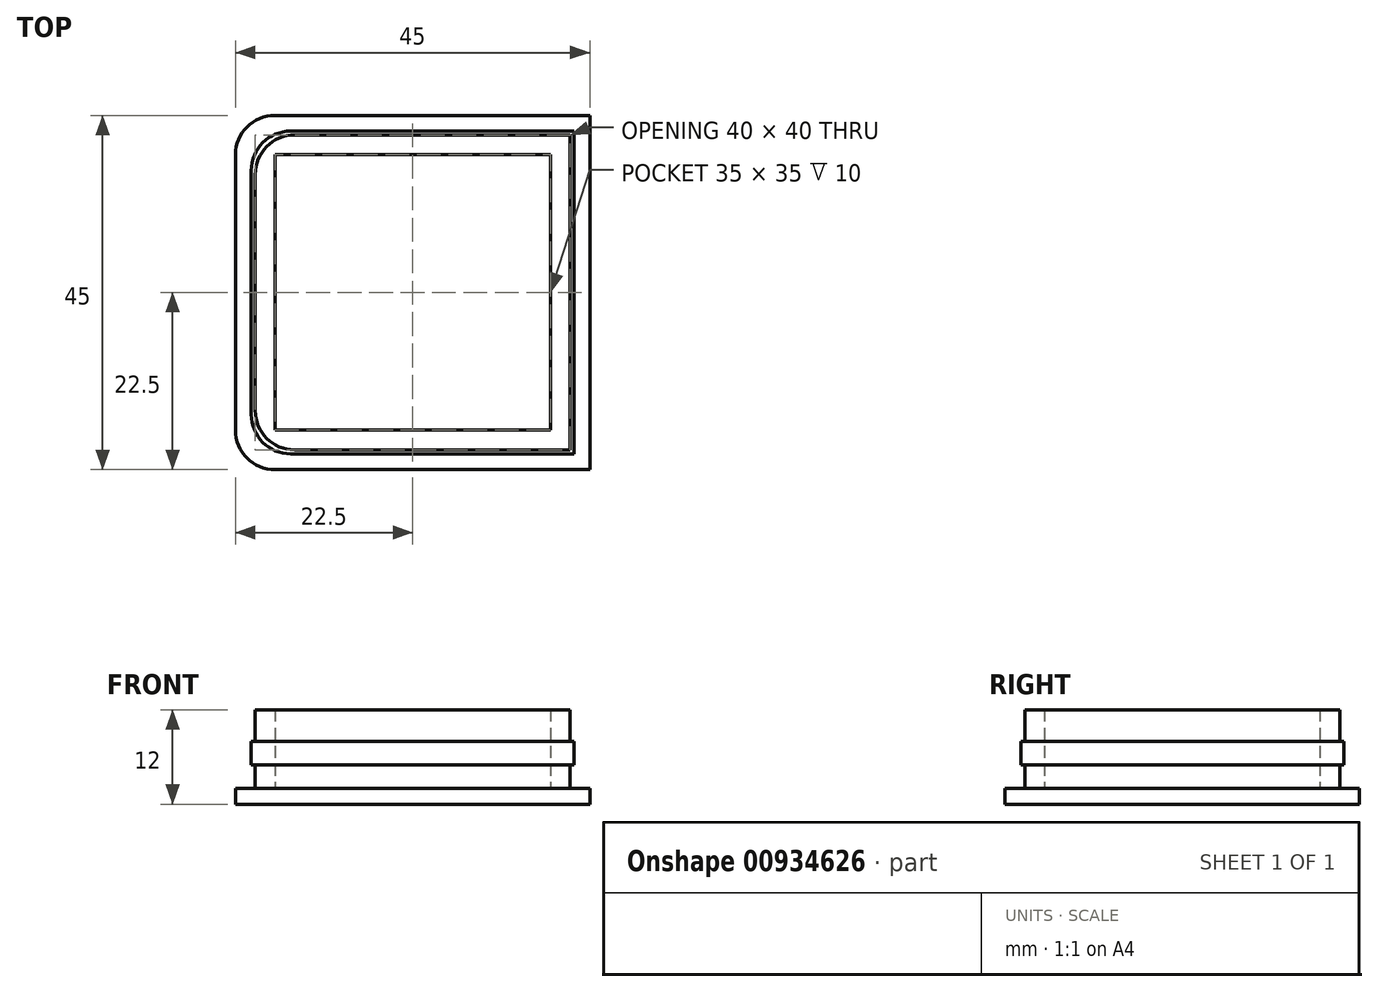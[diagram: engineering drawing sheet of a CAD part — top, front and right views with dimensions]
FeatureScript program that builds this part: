
annotation { "Feature Type Name" : "Feature", "Feature Type Description" : "" }
export const myFeature = defineFeature(function(context is Context, id is Id, definition is map)
    precondition{}
    {
        {
            var Q0;
            Q0=qCreatedBy(makeId("Top.planeOp"),FACE);
            var sketch = newSketch(context, id + "F0", { "sketchPlane" : qUnion([Q0])});
            skLineSegment(sketch, "E0.bottom", {"start": v(22.5, -22.5) * mm, "end": v(-22.5, -22.5) * mm});
            skLineSegment(sketch, "E0.top", {"start": v(22.5, 22.5) * mm, "end": v(-22.5, 22.5) * mm});
            skLineSegment(sketch, "E0.left", {"start": v(22.5, -22.5) * mm, "end": v(22.5, 22.5) * mm});
            skLineSegment(sketch, "E0.right", {"start": v(-22.5, -22.5) * mm, "end": v(-22.5, 22.5) * mm});
            skPoint(sketch, "E0.middle", {"position": v(0, 0) * mm});
            skSolve(sketch);
        }
        {
            var Q0;
            Q0=makeQuery(id+"F0.imprint","IMPRINT",FACE,{"disambiguationData":[TD([[makeQuery(id+"F0.imprint","IMPRINT",EDGE,{"derivedFrom":sQuery(id+"F0.wireOp",EDGE,"E0.bottom")}),-1.0]])]});
            extrude(context, id + "F1", {"entities" : qUnion([Q0]), "depth" : 2 * mm, "offsetDistance" : 25 * mm});
        }
        {
            var Q0;
            Q0=makeQuery(id+"F1.opExtrude","CAP_FACE",FACE,{"disambiguationData":[OSD([sQuery(id+"F0.wireOp",EDGE,"E0.bottom"),sQuery(id+"F0.wireOp",EDGE,"E0.top"),sQuery(id+"F0.wireOp",EDGE,"E0.left"),sQuery(id+"F0.wireOp",EDGE,"E0.right")])],"isStart":false});
            var sketch = newSketch(context, id + "F2", { "sketchPlane" : qUnion([Q0])});
            skLineSegment(sketch, "E1.bottom", {"start": v(-20, -20) * mm, "end": v(20, -20) * mm});
            skLineSegment(sketch, "E1.top", {"start": v(-20, 20) * mm, "end": v(20, 20) * mm});
            skLineSegment(sketch, "E1.left", {"start": v(-20, -20) * mm, "end": v(-20, 20) * mm});
            skLineSegment(sketch, "E1.right", {"start": v(20, -20) * mm, "end": v(20, 20) * mm});
            skPoint(sketch, "E1.middle", {"position": v(0, 0) * mm});
            skLineSegment(sketch, "E2.bottom", {"start": v(-17.5, -17.5) * mm, "end": v(17.5, -17.5) * mm});
            skLineSegment(sketch, "E2.top", {"start": v(-17.5, 17.5) * mm, "end": v(17.5, 17.5) * mm});
            skLineSegment(sketch, "E2.left", {"start": v(-17.5, -17.5) * mm, "end": v(-17.5, 17.5) * mm});
            skLineSegment(sketch, "E2.right", {"start": v(17.5, -17.5) * mm, "end": v(17.5, 17.5) * mm});
            skSolve(sketch);
        }
        {
            var Q0;
            Q0=makeQuery(id+"F2.imprint","IMPRINT",FACE,{"disambiguationData":[TD([[makeQuery(id+"F2.imprint","IMPRINT",EDGE,{"derivedFrom":sQuery(id+"F2.wireOp",EDGE,"E1.bottom")}),1.0]])]});
            extrude(context, id + "F3", {"entities" : qUnion([Q0]), "operationType" : NewBodyOperationType.ADD, "depth" : 10 * mm, "offsetDistance" : 25 * mm});
        }
        {
            var Q0;
            Q0=makeQuery(id+"F3.boolean.opBoolean","SPLIT",FACE,{"disambiguationData":[TD([makeQuery(id+"F3.opExtrude","SWEPT_FACE",FACE,{"disambiguationData":[OSD([sQuery(id+"F2.wireOp",EDGE,"E2.bottom")])]})])],"derivedFrom":makeQuery(id+"F1.opExtrude","CAP_FACE",FACE,{"disambiguationData":[OSD([sQuery(id+"F0.wireOp",EDGE,"E0.bottom"),sQuery(id+"F0.wireOp",EDGE,"E0.top"),sQuery(id+"F0.wireOp",EDGE,"E0.left"),sQuery(id+"F0.wireOp",EDGE,"E0.right")])],"isStart":false})});
            var sketch = newSketch(context, id + "F4", { "sketchPlane" : qUnion([Q0])});
            skLineSegment(sketch, "E3.bottom", {"start": v(-20.5, -20.5) * mm, "end": v(20.5, -20.5) * mm});
            skLineSegment(sketch, "E3.top", {"start": v(-20.5, 20.5) * mm, "end": v(20.5, 20.5) * mm});
            skLineSegment(sketch, "E3.left", {"start": v(-20.5, -20.5) * mm, "end": v(-20.5, 20.5) * mm});
            skLineSegment(sketch, "E3.right", {"start": v(20.5, -20.5) * mm, "end": v(20.5, 20.5) * mm});
            skPoint(sketch, "E3.middle", {"position": v(0, 0) * mm});
            skSolve(sketch);
        }
        {
            var Q0;
            Q0=makeQuery(id+"F4.imprint","IMPRINT",FACE,{"disambiguationData":[TD([[makeQuery(id+"F4.imprint","IMPRINT",EDGE,{"derivedFrom":sQuery(id+"F4.wireOp",EDGE,"E3.bottom")}),1.0]])]});
            extrude(context, id + "F5", {"entities" : qUnion([Q0]), "operationType" : NewBodyOperationType.ADD, "depth" : 6 * mm, "offsetDistance" : 25 * mm, "hasSecondDirection" : true, "secondDirectionOppositeDirection" : true, "secondDirectionDepth" : -3 * mm});
        }
        {
            var Q0;
            Q0=makeQuery(id+"F1.opExtrude","SWEPT_EDGE",EDGE,{"disambiguationData":[OSD([sQuery(id+"F0.wireOp",EDGE,"E0.top"),sQuery(id+"F0.wireOp",EDGE,"E0.right")])]});
            var Q1;
            {var subQ0=sQuery(id+"F2.wireOp",EDGE,"E1.left");var subQ1=sQuery(id+"F2.wireOp",EDGE,"E1.top");Q1=makeQuery(id+"F5.boolean.opBoolean","SPLIT",EDGE,{"disambiguationData":[TD([makeQuery(id+"F1.opExtrude","CAP_FACE",FACE,{"disambiguationData":[OSD([sQuery(id+"F0.wireOp",EDGE,"E0.bottom"),sQuery(id+"F0.wireOp",EDGE,"E0.top"),sQuery(id+"F0.wireOp",EDGE,"E0.left"),sQuery(id+"F0.wireOp",EDGE,"E0.right")])],"isStart":false})])],"derivedFrom":makeQuery(id+"F3.opExtrude","SWEPT_EDGE",EDGE,{"disambiguationData":[OSD([subQ1,subQ0])]})});}
            var Q2;
            Q2=makeQuery(id+"F5.opExtrude","SWEPT_EDGE",EDGE,{"disambiguationData":[OSD([sQuery(id+"F4.wireOp",EDGE,"E3.top"),sQuery(id+"F4.wireOp",EDGE,"E3.left")])]});
            var Q3;
            {var subQ0=sQuery(id+"F2.wireOp",EDGE,"E2.right");var subQ1=sQuery(id+"F2.wireOp",EDGE,"E2.left");var subQ2=sQuery(id+"F2.wireOp",EDGE,"E2.top");var subQ3=sQuery(id+"F2.wireOp",EDGE,"E2.bottom");var subQ4=sQuery(id+"F2.wireOp",EDGE,"E1.left");var subQ5=sQuery(id+"F2.wireOp",EDGE,"E1.top");Q3=makeQuery(id+"F5.boolean.opBoolean","SPLIT",EDGE,{"disambiguationData":[TD([makeQuery(id+"F3.opExtrude","CAP_FACE",FACE,{"disambiguationData":[OSD([sQuery(id+"F2.wireOp",EDGE,"E1.bottom"),subQ5,subQ4,sQuery(id+"F2.wireOp",EDGE,"E1.right"),subQ3,subQ2,subQ1,subQ0])],"isStart":false})])],"derivedFrom":makeQuery(id+"F3.opExtrude","SWEPT_EDGE",EDGE,{"disambiguationData":[OSD([subQ5,subQ4])]})});}
            var Q4;
            Q4=makeQuery(id+"F1.opExtrude","SWEPT_EDGE",EDGE,{"disambiguationData":[OSD([sQuery(id+"F0.wireOp",EDGE,"E0.bottom"),sQuery(id+"F0.wireOp",EDGE,"E0.right")])]});
            var Q5;
            {var subQ0=sQuery(id+"F2.wireOp",EDGE,"E1.left");var subQ1=sQuery(id+"F2.wireOp",EDGE,"E1.bottom");Q5=makeQuery(id+"F5.boolean.opBoolean","SPLIT",EDGE,{"disambiguationData":[TD([makeQuery(id+"F1.opExtrude","CAP_FACE",FACE,{"disambiguationData":[OSD([sQuery(id+"F0.wireOp",EDGE,"E0.bottom"),sQuery(id+"F0.wireOp",EDGE,"E0.top"),sQuery(id+"F0.wireOp",EDGE,"E0.left"),sQuery(id+"F0.wireOp",EDGE,"E0.right")])],"isStart":false})])],"derivedFrom":makeQuery(id+"F3.opExtrude","SWEPT_EDGE",EDGE,{"disambiguationData":[OSD([subQ1,subQ0])]})});}
            var Q6;
            Q6=makeQuery(id+"F5.opExtrude","SWEPT_EDGE",EDGE,{"disambiguationData":[OSD([sQuery(id+"F4.wireOp",EDGE,"E3.bottom"),sQuery(id+"F4.wireOp",EDGE,"E3.left")])]});
            var Q7;
            {var subQ0=sQuery(id+"F2.wireOp",EDGE,"E1.bottom");var subQ1=sQuery(id+"F2.wireOp",EDGE,"E2.right");var subQ2=sQuery(id+"F2.wireOp",EDGE,"E2.left");var subQ3=sQuery(id+"F2.wireOp",EDGE,"E2.top");var subQ4=sQuery(id+"F2.wireOp",EDGE,"E2.bottom");var subQ5=sQuery(id+"F2.wireOp",EDGE,"E1.left");Q7=makeQuery(id+"F5.boolean.opBoolean","SPLIT",EDGE,{"disambiguationData":[TD([makeQuery(id+"F3.opExtrude","CAP_FACE",FACE,{"disambiguationData":[OSD([subQ0,sQuery(id+"F2.wireOp",EDGE,"E1.top"),subQ5,sQuery(id+"F2.wireOp",EDGE,"E1.right"),subQ4,subQ3,subQ2,subQ1])],"isStart":false})])],"derivedFrom":makeQuery(id+"F3.opExtrude","SWEPT_EDGE",EDGE,{"disambiguationData":[OSD([subQ0,subQ5])]})});}
            fillet(context, id + "F6", {"entities" : qUnion([Q0, Q1, Q2, Q3, Q4, Q5, Q6, Q7]), "radius" : 5 * mm, "tangentPropagation" : true, "allowEdgeOverflow" : false});
        }
    });
